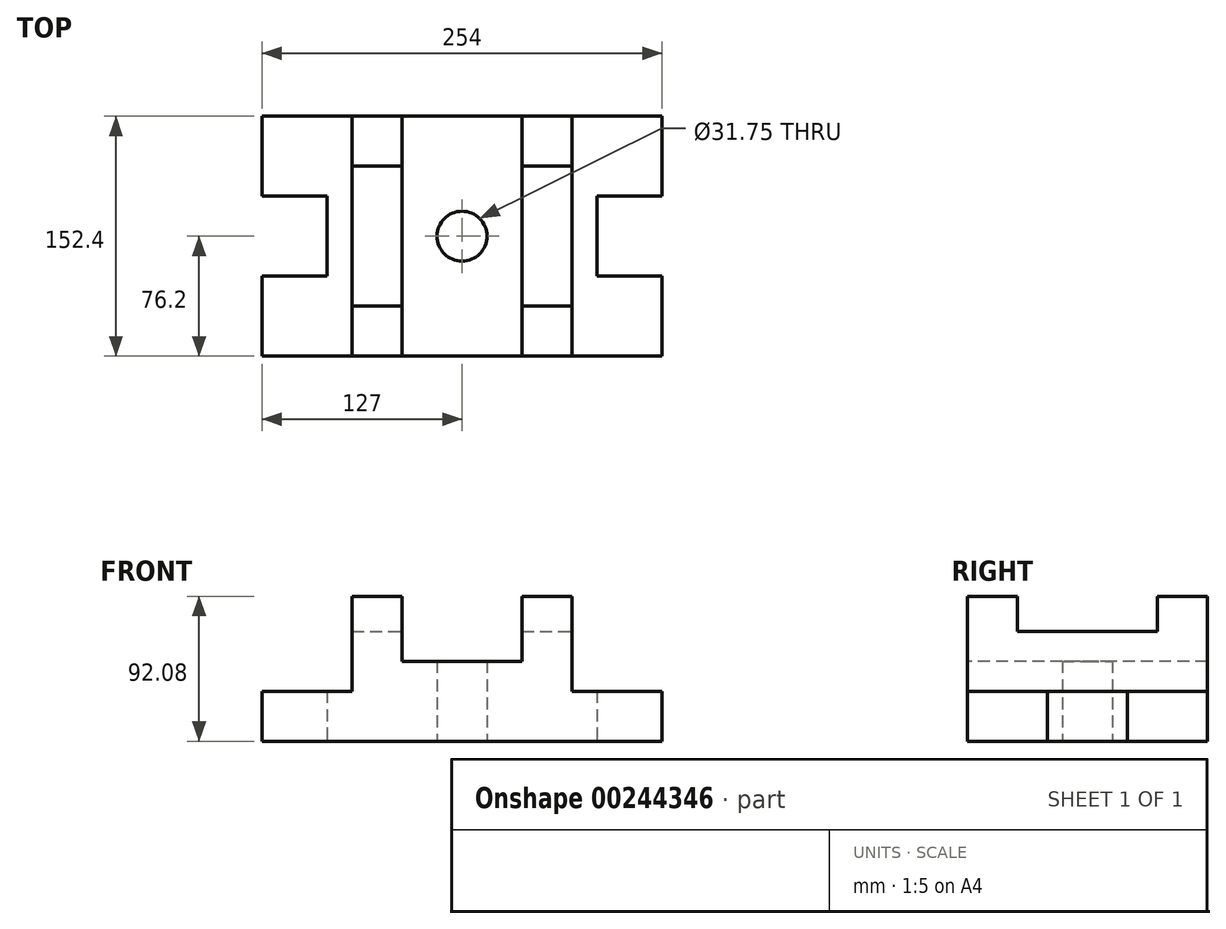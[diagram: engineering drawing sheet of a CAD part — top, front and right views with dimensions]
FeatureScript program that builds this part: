
annotation { "Feature Type Name" : "Feature", "Feature Type Description" : "" }
export const myFeature = defineFeature(function(context is Context, id is Id, definition is map)
    precondition{}
    {
        {
            var Q0;
            Q0=qCreatedBy(makeId("Top.planeOp"),FACE);
            var sketch = newSketch(context, id + "F0", { "sketchPlane" : qUnion([Q0])});
            skLineSegment(sketch, "E0.bottom", {"start": v(-127, 76.2) * mm, "end": v(127, 76.2) * mm});
            skLineSegment(sketch, "E0.top", {"start": v(-127, -76.2) * mm, "end": v(127, -76.2) * mm});
            skLineSegment(sketch, "E0.left", {"start": v(-127, 76.2) * mm, "end": v(-127, 25.4) * mm});
            skLineSegment(sketch, "E0.right", {"start": v(127, 76.2) * mm, "end": v(127, 25.4) * mm});
            skPoint(sketch, "E0.middle", {"position": v(0, 0) * mm});
            skLineSegment(sketch, "E1", {"start": v(-127, 25.4) * mm, "end": v(-85.72, 25.4) * mm});
            skLineSegment(sketch, "E2", {"start": v(-85.72, -25.4) * mm, "end": v(-85.72, 25.4) * mm});
            skLineSegment(sketch, "E3", {"start": v(-85.72, -25.4) * mm, "end": v(-127, -25.4) * mm});
            skLineSegment(sketch, "E4", {"start": v(127, 25.4) * mm, "end": v(85.72, 25.4) * mm});
            skLineSegment(sketch, "E5", {"start": v(85.72, -25.4) * mm, "end": v(85.72, 25.4) * mm});
            skLineSegment(sketch, "E6", {"start": v(85.72, -25.4) * mm, "end": v(127, -25.4) * mm});
            skLineSegment(sketch, "E7", {"start": v(-69.85, 76.2) * mm, "end": v(-69.85, -76.2) * mm});
            skLineSegment(sketch, "E8", {"start": v(-38.1, 76.2) * mm, "end": v(-38.1, -76.2) * mm});
            skLineSegment(sketch, "E9", {"start": v(69.85, 76.2) * mm, "end": v(69.85, -76.2) * mm});
            skLineSegment(sketch, "E10", {"start": v(38.1, 76.2) * mm, "end": v(38.1, -76.2) * mm});
            skLineSegment(sketch, "E11.trimOffspring", {"start": v(-127, -25.4) * mm, "end": v(-127, -76.2) * mm});
            skLineSegment(sketch, "E12.trimOffspring", {"start": v(127, -25.4) * mm, "end": v(127, -76.2) * mm});
            skCircle(sketch, "E13", {"center": v(0, 0) * mm, "radius": 15.88 * mm});
            skLineSegment(sketch, "E14", {"start": v(-69.85, 44.45) * mm, "end": v(-38.1, 44.45) * mm});
            skLineSegment(sketch, "E15", {"start": v(-69.85, -44.45) * mm, "end": v(-38.1, -44.45) * mm});
            skLineSegment(sketch, "E16", {"start": v(38.1, -44.45) * mm, "end": v(69.85, -44.45) * mm});
            skLineSegment(sketch, "E17", {"start": v(38.1, 44.45) * mm, "end": v(69.85, 44.45) * mm});
            skSolve(sketch);
        }
        {
            var Q0;
            {var subQ4=sQuery(id+"F0.wireOp",EDGE,"E0.left");Q0=makeQuery(id+"F0.imprint","IMPRINT",FACE,{"disambiguationData":[TD([[makeQuery(id+"F0.imprint","IMPRINT",EDGE,{"derivedFrom":subQ4}),1.0]])]});}
            var Q1;
            {var subQ4=sQuery(id+"F0.wireOp",EDGE,"E0.right");Q1=makeQuery(id+"F0.imprint","IMPRINT",FACE,{"disambiguationData":[TD([[makeQuery(id+"F0.imprint","IMPRINT",EDGE,{"derivedFrom":subQ4}),-1.0]])]});}
            extrude(context, id + "F1", {"entities" : qUnion([Q0, Q1]), "depth" : 31.75 * mm});
        }
        {
            var Q0;
            {var subQ0=sQuery(id+"F0.wireOp",EDGE,"E14");Q0=makeQuery(id+"F0.imprint","IMPRINT",FACE,{"disambiguationData":[TD([[makeQuery(id+"F0.imprint","IMPRINT",EDGE,{"derivedFrom":subQ0}),-1.0]])]});}
            var Q1;
            {var subQ0=sQuery(id+"F0.wireOp",EDGE,"E16");Q1=makeQuery(id+"F0.imprint","IMPRINT",FACE,{"disambiguationData":[TD([[makeQuery(id+"F0.imprint","IMPRINT",EDGE,{"derivedFrom":subQ0}),1.0]])]});}
            extrude(context, id + "F2", {"entities" : qUnion([Q0, Q1]), "operationType" : NewBodyOperationType.ADD, "depth" : 69.85 * mm});
        }
        {
            var Q0;
            {var subQ5=sQuery(id+"F0.wireOp",EDGE,"E14");Q0=makeQuery(id+"F0.imprint","IMPRINT",FACE,{"disambiguationData":[TD([[makeQuery(id+"F0.imprint","IMPRINT",EDGE,{"derivedFrom":subQ5}),1.0]])]});}
            var Q1;
            {var subQ5=sQuery(id+"F0.wireOp",EDGE,"E15");Q1=makeQuery(id+"F0.imprint","IMPRINT",FACE,{"disambiguationData":[TD([[makeQuery(id+"F0.imprint","IMPRINT",EDGE,{"derivedFrom":subQ5}),-1.0]])]});}
            var Q2;
            {var subQ5=sQuery(id+"F0.wireOp",EDGE,"E16");Q2=makeQuery(id+"F0.imprint","IMPRINT",FACE,{"disambiguationData":[TD([[makeQuery(id+"F0.imprint","IMPRINT",EDGE,{"derivedFrom":subQ5}),-1.0]])]});}
            var Q3;
            {var subQ5=sQuery(id+"F0.wireOp",EDGE,"E17");Q3=makeQuery(id+"F0.imprint","IMPRINT",FACE,{"disambiguationData":[TD([[makeQuery(id+"F0.imprint","IMPRINT",EDGE,{"derivedFrom":subQ5}),1.0]])]});}
            extrude(context, id + "F3", {"entities" : qUnion([Q0, Q1, Q2, Q3]), "operationType" : NewBodyOperationType.ADD, "depth" : 92.07 * mm});
        }
        {
            var Q0;
            Q0=makeQuery(id+"F0.imprint","IMPRINT",FACE,{"disambiguationData":[TD([[makeQuery(id+"F0.imprint","IMPRINT",EDGE,{"derivedFrom":sQuery(id+"F0.wireOp",EDGE,"E13")}),-1.0]])]});
            extrude(context, id + "F4", {"entities" : qUnion([Q0]), "operationType" : NewBodyOperationType.ADD, "depth" : 50.8 * mm});
        }
    });
